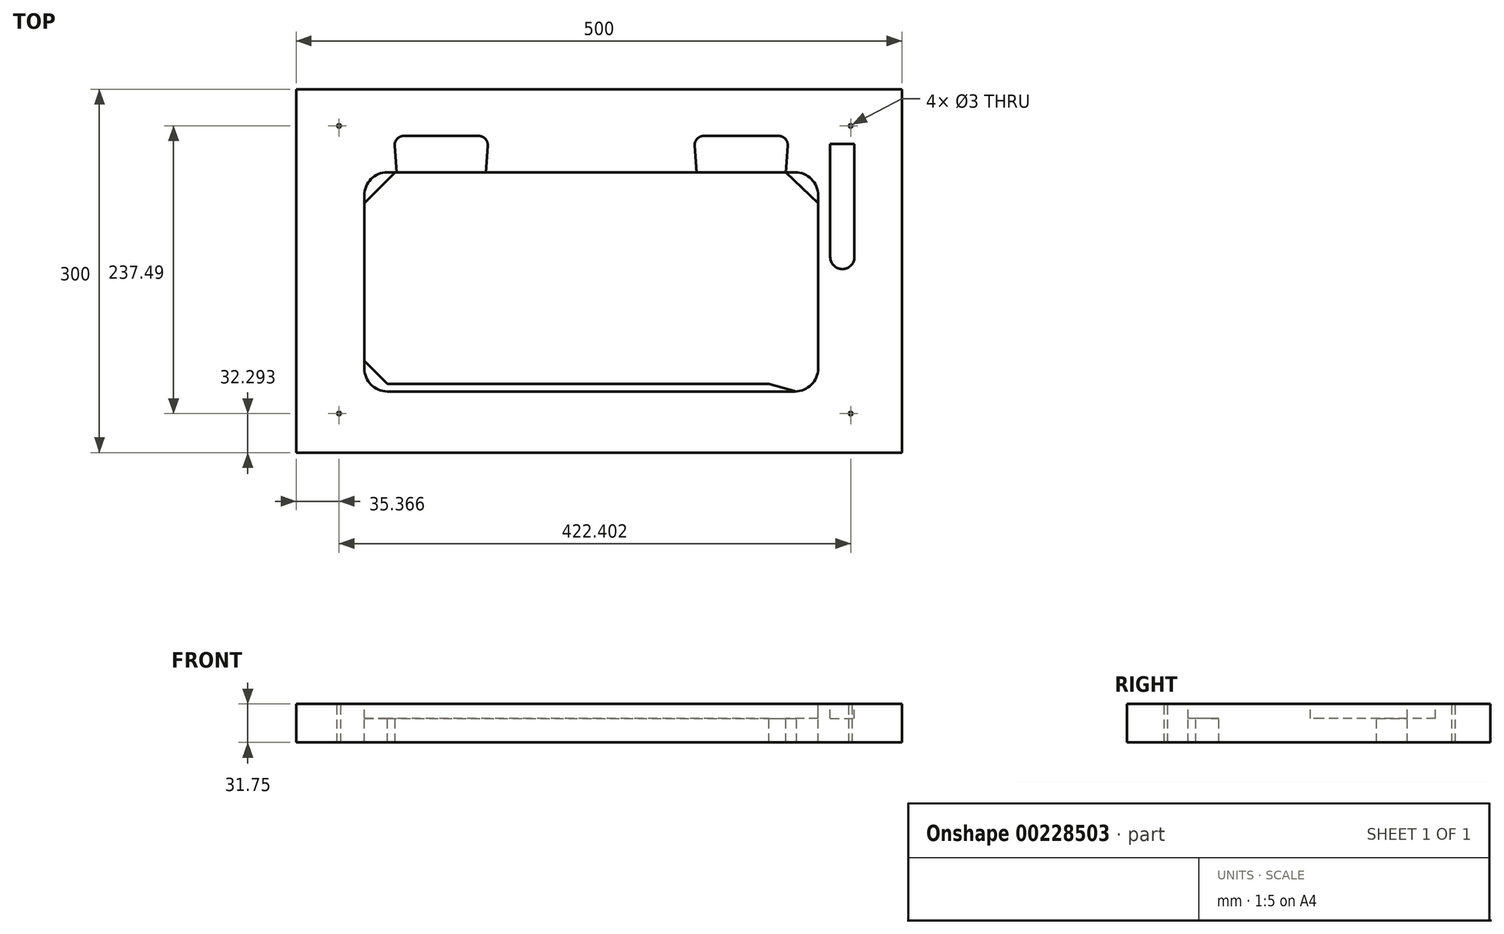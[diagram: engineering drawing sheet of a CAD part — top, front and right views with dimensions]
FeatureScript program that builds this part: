
annotation { "Feature Type Name" : "Feature", "Feature Type Description" : "" }
export const myFeature = defineFeature(function(context is Context, id is Id, definition is map)
    precondition{}
    {
        {
            var Q0;
            Q0=qCreatedBy(makeId("Top.planeOp"),FACE);
            var sketch = newSketch(context, id + "F0", { "sketchPlane" : qUnion([Q0])});
            skLineSegment(sketch, "E0.bottom", {"start": v(-250, -150) * mm, "end": v(250, -150) * mm});
            skLineSegment(sketch, "E0.top", {"start": v(-250, 150) * mm, "end": v(250, 150) * mm});
            skLineSegment(sketch, "E0.left", {"start": v(-250, -150) * mm, "end": v(-250, 150) * mm});
            skLineSegment(sketch, "E0.right", {"start": v(250, -150) * mm, "end": v(250, 150) * mm});
            skSolve(sketch);
        }
        {
            var Q0;
            Q0 = qSketchRegion(id + "F0", true);
            extrude(context, id + "F1", {"entities" : qUnion([Q0]), "oppositeDirection" : true, "depth" : 31.75 * mm});
        }
        {
            var Q0;
            Q0=qCreatedBy(makeId("Top.planeOp"),FACE);
            var sketch = newSketch(context, id + "F2", { "sketchPlane" : qUnion([Q0])});
            skCircle(sketch, "E1", {"center": v(-214.63, 119.78) * mm, "radius": 1.5 * mm});
            skCircle(sketch, "E2.0.1.0", {"center": v(-214.63, -117.7) * mm, "radius": 1.5 * mm});
            skCircle(sketch, "E2.1.0.0", {"center": v(207.77, 119.78) * mm, "radius": 1.5 * mm});
            skCircle(sketch, "E2.1.1.0", {"center": v(207.77, -117.7) * mm, "radius": 1.5 * mm});
            skCircle(sketch, "E2.2.0.0", {"center": v(630.17, 119.78) * mm, "radius": 1.5 * mm});
            skCircle(sketch, "E2.2.1.0", {"center": v(630.17, -117.7) * mm, "radius": 1.5 * mm});
            skLineSegment(sketch, "E2.direction1", {"start": v(-214.63, 119.78) * mm, "end": v(207.77, 119.78) * mm, "construction": true});
            skLineSegment(sketch, "E2.direction2", {"start": v(-214.63, 119.78) * mm, "end": v(-214.63, -117.7) * mm, "construction": true});
            skSolve(sketch);
        }
        {
            var Q0;
            Q0 = qSketchRegion(id + "F2", true);
            extrude(context, id + "F3", {"entities" : qUnion([Q0]), "operationType" : NewBodyOperationType.REMOVE, "endBound" : BoundingType.THROUGH_ALL, "oppositeDirection" : true, "depth" : 25.4 * mm});
        }
        {
            var Q0;
            Q0=qCreatedBy(makeId("Top.planeOp"),FACE);
            var sketch = newSketch(context, id + "F4", { "sketchPlane" : qUnion([Q0])});
            skLineSegment(sketch, "E3.bottom", {"start": v(-174.7, -99.48) * mm, "end": v(161.84, -99.48) * mm});
            skLineSegment(sketch, "E3.top", {"start": v(-174.7, 81.5) * mm, "end": v(161.84, 81.5) * mm});
            skLineSegment(sketch, "E3.left", {"start": v(-193.76, -80.43) * mm, "end": v(-193.76, 62.45) * mm});
            skLineSegment(sketch, "E3.right", {"start": v(180.9, -80.43) * mm, "end": v(180.9, 62.45) * mm});
            skPoint(sketch, "E4.visualSharp", {"position": v(-193.76, 81.5) * mm});
            skArc(sketch, "E4.filletArc", {"start": v(-174.7, 81.5) * mm, "mid": v(-188.18, 75.92) * mm, "end": v(-193.76, 62.45) * mm});
            skPoint(sketch, "E5.visualSharp", {"position": v(-193.76, -99.48) * mm});
            skArc(sketch, "E5.filletArc", {"start": v(-193.76, -80.43) * mm, "mid": v(-188.18, -93.9) * mm, "end": v(-174.7, -99.48) * mm});
            skPoint(sketch, "E6.visualSharp", {"position": v(180.9, -99.48) * mm});
            skArc(sketch, "E6.filletArc", {"start": v(161.84, -99.48) * mm, "mid": v(175.31, -93.9) * mm, "end": v(180.9, -80.43) * mm});
            skPoint(sketch, "E7.visualSharp", {"position": v(180.9, 81.5) * mm});
            skArc(sketch, "E7.filletArc", {"start": v(180.9, 62.45) * mm, "mid": v(175.31, 75.92) * mm, "end": v(161.84, 81.5) * mm});
            skLineSegment(sketch, "E8.bottom", {"start": v(190.9, 104.84) * mm, "end": v(210.9, 104.84) * mm});
            skLineSegment(sketch, "E8.left", {"start": v(190.9, 104.84) * mm, "end": v(190.9, 11.5) * mm});
            skLineSegment(sketch, "E8.right", {"start": v(210.9, 104.84) * mm, "end": v(210.9, 11.5) * mm});
            skArc(sketch, "E9", {"start": v(190.9, 11.5) * mm, "mid": v(200.9, 1.5) * mm, "end": v(210.9, 11.5) * mm});
            skSolve(sketch);
        }
        {
            var Q0;
            Q0 = qSketchRegion(id + "F4", true);
            extrude(context, id + "F5", {"entities" : qUnion([Q0]), "operationType" : NewBodyOperationType.REMOVE, "oppositeDirection" : true, "depth" : 12 * mm});
        }
        {
            var Q0;
            Q0=qCreatedBy(makeId("Top.planeOp"),FACE);
            var sketch = newSketch(context, id + "F6", { "sketchPlane" : qUnion([Q0])});
            skLineSegment(sketch, "E10", {"start": v(-168.72, 103.31) * mm, "end": v(-167.09, 81.5) * mm});
            skLineSegment(sketch, "E11", {"start": v(-167.09, 81.5) * mm, "end": v(-93.43, 81.5) * mm});
            skLineSegment(sketch, "E12", {"start": v(-93.43, 81.5) * mm, "end": v(-91.8, 103.31) * mm});
            skLineSegment(sketch, "E13", {"start": v(-99.4, 111.5) * mm, "end": v(-161.12, 111.5) * mm});
            skPoint(sketch, "E14.visualSharp", {"position": v(-169.33, 111.5) * mm});
            skArc(sketch, "E14.filletArc", {"start": v(-161.12, 111.5) * mm, "mid": v(-166.7, 109.06) * mm, "end": v(-168.72, 103.31) * mm});
            skPoint(sketch, "E15.visualSharp", {"position": v(-91.19, 111.5) * mm});
            skArc(sketch, "E15.filletArc", {"start": v(-91.8, 103.31) * mm, "mid": v(-93.81, 109.06) * mm, "end": v(-99.4, 111.5) * mm});
            skLineSegment(sketch, "E16", {"start": v(-130.26, 111.5) * mm, "end": v(-130.26, 81.5) * mm, "construction": true});
            skLineSegment(sketch, "E17", {"start": v(-6.43, 113.09) * mm, "end": v(-6.43, 49.91) * mm, "construction": true});
            skPoint(sketch, "E18.MirrorP", {"position": v(156.46, 111.5) * mm});
            skLineSegment(sketch, "E19.MirrorCS", {"start": v(86.53, 111.5) * mm, "end": v(148.25, 111.5) * mm});
            skLineSegment(sketch, "E20.MirrorCS", {"start": v(155.85, 103.31) * mm, "end": v(154.22, 81.5) * mm});
            skLineSegment(sketch, "E21.MirrorCS", {"start": v(80.56, 81.5) * mm, "end": v(78.93, 103.31) * mm});
            skLineSegment(sketch, "E22.MirrorCS", {"start": v(154.22, 81.5) * mm, "end": v(80.56, 81.5) * mm});
            skArc(sketch, "E23.MirrorCS", {"start": v(78.93, 103.31) * mm, "mid": v(80.94, 109.06) * mm, "end": v(86.53, 111.5) * mm});
            skLineSegment(sketch, "E24.MirrorCS", {"start": v(117.4, 111.5) * mm, "end": v(117.4, 81.5) * mm, "construction": true});
            skArc(sketch, "E25.MirrorCS", {"start": v(148.25, 111.5) * mm, "mid": v(153.84, 109.06) * mm, "end": v(155.85, 103.31) * mm});
            skPoint(sketch, "E26.MirrorP", {"position": v(78.32, 111.5) * mm});
            skSolve(sketch);
        }
        {
            var Q0;
            Q0=makeQuery(id+"F4.imprint","IMPRINT",FACE,{"disambiguationData":[TD([[makeQuery(id+"F4.imprint","IMPRINT",EDGE,{"derivedFrom":sQuery(id+"F4.wireOp",EDGE,"E3.bottom")}),1.0]])]});
            var sketch = newSketch(context, id + "F7", { "sketchPlane" : qUnion([Q0])});
            skPoint(sketch, "E27.visualSharp", {"position": v(-187.4, 75.15) * mm});
            skLineSegment(sketch, "E28", {"start": v(140.17, -93.13) * mm, "end": v(-174.7, -93.13) * mm});
            skLineSegment(sketch, "E29.bottom", {"start": v(-168.36, 81.5) * mm, "end": v(154.22, 81.5) * mm});
            skLineSegment(sketch, "E30", {"start": v(-193.76, 56.1) * mm, "end": v(-187.4, 62.45) * mm});
            skLineSegment(sketch, "E31", {"start": v(-193.76, -74.08) * mm, "end": v(-174.7, -93.13) * mm});
            skLineSegment(sketch, "E32", {"start": v(-193.76, 56.1) * mm, "end": v(-193.76, -74.08) * mm});
            skLineSegment(sketch, "E33", {"start": v(-187.4, 62.45) * mm, "end": v(-168.36, 81.5) * mm});
            skLineSegment(sketch, "E34", {"start": v(180.9, 56.1) * mm, "end": v(154.22, 81.5) * mm});
            skLineSegment(sketch, "E35", {"start": v(180.9, 56.1) * mm, "end": v(180.9, -80.43) * mm});
            skArc(sketch, "E36", {"start": v(163.03, -99.44) * mm, "mid": v(175.72, -93.47) * mm, "end": v(180.9, -80.43) * mm});
            skLineSegment(sketch, "E37", {"start": v(140.17, -93.13) * mm, "end": v(163.03, -99.44) * mm});
            skSolve(sketch);
        }
        {
            var Q0;
            Q0 = qSketchRegion(id + "F7", true);
            extrude(context, id + "F8", {"entities" : qUnion([Q0]), "operationType" : NewBodyOperationType.REMOVE, "endBound" : BoundingType.THROUGH_ALL, "oppositeDirection" : true, "depth" : 25.4 * mm});
        }
        {
            var Q0;
            Q0 = qSketchRegion(id + "F6", true);
            extrude(context, id + "F9", {"entities" : qUnion([Q0]), "operationType" : NewBodyOperationType.REMOVE, "oppositeDirection" : true, "depth" : 3 / 101.6 * mm});
        }
    });
